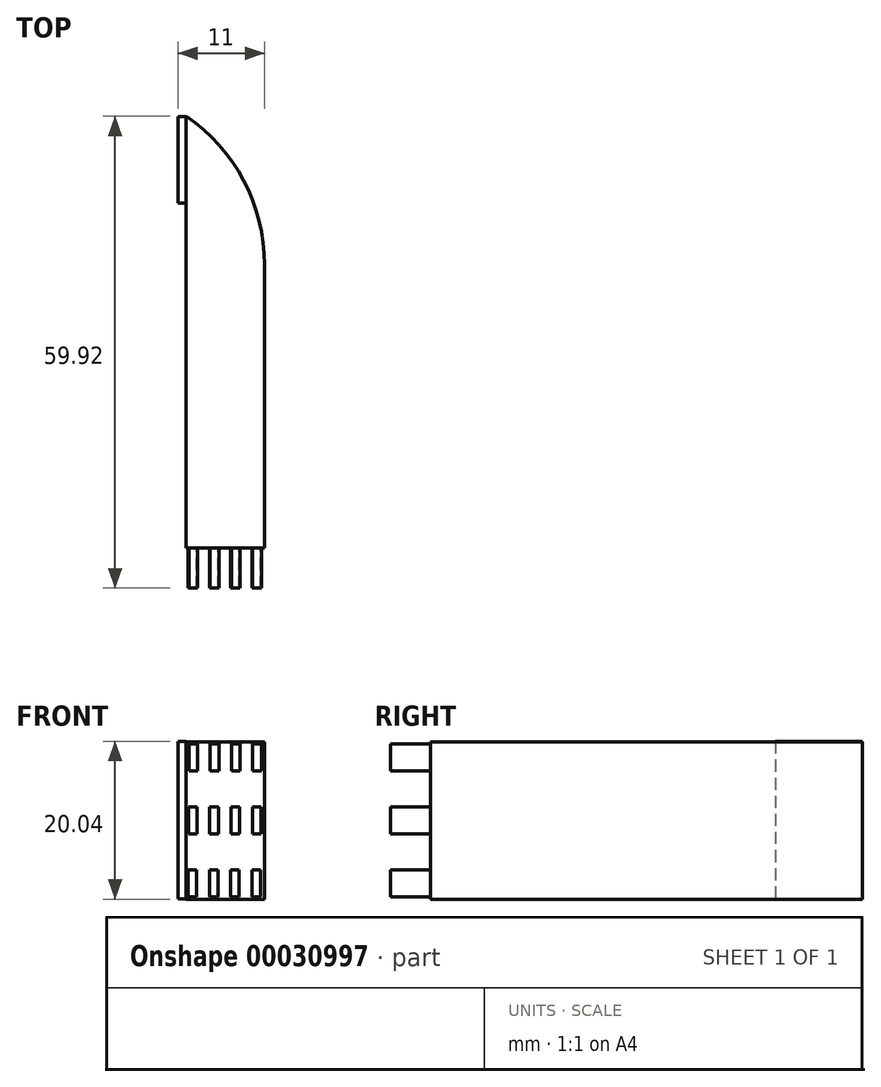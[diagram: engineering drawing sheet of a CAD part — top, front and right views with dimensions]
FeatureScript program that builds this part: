
annotation { "Feature Type Name" : "Feature", "Feature Type Description" : "" }
export const myFeature = defineFeature(function(context is Context, id is Id, definition is map)
    precondition{}
    {
        {
            var Q0;
            Q0=qCreatedBy(makeId("Front.planeOp"),FACE);
            var sketch = newSketch(context, id + "F0", { "sketchPlane" : qUnion([Q0])});
            skLineSegment(sketch, "E0.rect.bottom", {"start": v(-5, 10) * mm, "end": v(5, 10) * mm});
            skLineSegment(sketch, "E0.rect.top", {"start": v(-5, -10) * mm, "end": v(5, -10) * mm});
            skLineSegment(sketch, "E0.rect.left", {"start": v(-5, 10) * mm, "end": v(-5, -10) * mm});
            skLineSegment(sketch, "E0.rect.right", {"start": v(5, 10) * mm, "end": v(5, -10) * mm});
            skPoint(sketch, "E0.rect.middle", {"position": v(0, 0) * mm});
            skSolve(sketch);
        }
        {
            var Q0;
            Q0 = qSketchRegion(id + "F0", true);
            extrude(context, id + "F1", {"entities" : qUnion([Q0]), "oppositeDirection" : true, "depth" : 25 * mm});
        }
        {
            var Q0;
            Q0=makeQuery(id+"F1.opExtrude","CAP_EDGE",EDGE,{"disambiguationData":[OSD([sQuery(id+"F0.wireOp",EDGE,"E0.rect.left")])],"isStart":false});
            cPlane(context, id + "F2", {"entities" : qUnion([Q0]), "cplaneType" : CPlaneType.LINE_ANGLE, "offset" : 150 * mm, "angle" : 0 * degree, "width" : 150 * mm, "height" : 150 * mm});
        }
        {
            var Q0;
            Q0=qCreatedBy(id+"F2.planeOp",FACE);
            var sketch = newSketch(context, id + "F3", { "sketchPlane" : qUnion([Q0])});
            skLineSegment(sketch, "E1.rect.bottom", {"start": v(-54.87, 10) * mm, "end": v(-24.87, 10) * mm});
            skLineSegment(sketch, "E1.rect.top", {"start": v(-54.87, -10) * mm, "end": v(-24.87, -10) * mm});
            skLineSegment(sketch, "E1.rect.left", {"start": v(-54.87, 10) * mm, "end": v(-54.87, -10) * mm});
            skLineSegment(sketch, "E1.rect.right", {"start": v(-24.87, 10) * mm, "end": v(-24.87, -10) * mm});
            skPoint(sketch, "E1.rect.middle", {"position": v(-39.87, 0) * mm});
            skSolve(sketch);
        }
        {
            var Q0;
            Q0=makeQuery(id+"F3.imprint","IMPRINT",FACE,{"disambiguationData":[TD([[makeQuery(id+"F3.imprint","IMPRINT",EDGE,{"derivedFrom":sQuery(id+"F3.wireOp",EDGE,"E1.rect.bottom")}),-1.0]])]});
            extrude(context, id + "F4", {"entities" : qUnion([Q0]), "operationType" : NewBodyOperationType.ADD, "oppositeDirection" : true, "depth" : 10 * mm});
        }
        {
            var Q0;
            Q0=makeQuery(id+"F4.opExtrude","CAP_EDGE",EDGE,{"disambiguationData":[OSD([sQuery(id+"F3.wireOp",EDGE,"E1.rect.left")])],"isStart":false});
            fillet(context, id + "F5", {"entities" : qUnion([Q0]), "radius" : 22.72 * mm, "tangentPropagation" : true, "allowEdgeOverflow" : false});
        }
        {
            var Q0;
            Q0=qCreatedBy(id+"F2.planeOp",FACE);
            var sketch = newSketch(context, id + "F6", { "sketchPlane" : qUnion([Q0])});
            skLineSegment(sketch, "E2.bottom", {"start": v(-54.82, 10.04) * mm, "end": v(-43.82, 10.04) * mm});
            skLineSegment(sketch, "E2.top", {"start": v(-54.82, -9.96) * mm, "end": v(-43.82, -9.96) * mm});
            skLineSegment(sketch, "E2.left", {"start": v(-54.82, 10.04) * mm, "end": v(-54.82, -9.96) * mm});
            skLineSegment(sketch, "E2.right", {"start": v(-43.82, 10.04) * mm, "end": v(-43.82, -9.96) * mm});
            skSolve(sketch);
        }
        {
            var Q0;
            Q0=makeQuery(id+"F6.imprint","IMPRINT",FACE,{"disambiguationData":[TD([[makeQuery(id+"F6.imprint","IMPRINT",EDGE,{"derivedFrom":sQuery(id+"F6.wireOp",EDGE,"E2.bottom")}),-1.0]])]});
            extrude(context, id + "F7", {"entities" : qUnion([Q0]), "operationType" : NewBodyOperationType.ADD, "depth" : 1 * mm});
        }
        {
            var Q0;
            Q0=makeQuery(id+"F1.opExtrude","CAP_FACE",FACE,{"disambiguationData":[OSD([sQuery(id+"F0.wireOp",EDGE,"E0.rect.bottom"),sQuery(id+"F0.wireOp",EDGE,"E0.rect.top"),sQuery(id+"F0.wireOp",EDGE,"E0.rect.left"),sQuery(id+"F0.wireOp",EDGE,"E0.rect.right")])],"isStart":true});
            var sketch = newSketch(context, id + "F8", { "sketchPlane" : qUnion([Q0])});
            skLineSegment(sketch, "E3.bottom", {"start": v(-4.6, 9.7) * mm, "end": v(-3.5, 9.7) * mm});
            skLineSegment(sketch, "E3.top", {"start": v(-4.6, 6.3) * mm, "end": v(-3.5, 6.3) * mm});
            skLineSegment(sketch, "E3.left", {"start": v(-4.6, 9.7) * mm, "end": v(-4.6, 6.3) * mm});
            skLineSegment(sketch, "E3.right", {"start": v(-3.5, 9.7) * mm, "end": v(-3.5, 6.3) * mm});
            skLineSegment(sketch, "E4.1.0.0", {"start": v(-0.8, 9.7) * mm, "end": v(-0.8, 6.3) * mm});
            skLineSegment(sketch, "E4.1.0.1", {"start": v(-1.9, 9.7) * mm, "end": v(-0.8, 9.7) * mm});
            skLineSegment(sketch, "E4.1.0.2", {"start": v(-1.9, 9.7) * mm, "end": v(-1.9, 6.3) * mm});
            skLineSegment(sketch, "E4.1.0.3", {"start": v(-1.9, 6.3) * mm, "end": v(-0.8, 6.3) * mm});
            skLineSegment(sketch, "E4.2.0.0", {"start": v(1.9, 9.7) * mm, "end": v(1.9, 6.3) * mm});
            skLineSegment(sketch, "E4.2.0.1", {"start": v(0.8, 9.7) * mm, "end": v(1.9, 9.7) * mm});
            skLineSegment(sketch, "E4.2.0.2", {"start": v(0.8, 9.7) * mm, "end": v(0.8, 6.3) * mm});
            skLineSegment(sketch, "E4.2.0.3", {"start": v(0.8, 6.3) * mm, "end": v(1.9, 6.3) * mm});
            skLineSegment(sketch, "E4.3.0.0", {"start": v(4.6, 9.7) * mm, "end": v(4.6, 6.3) * mm});
            skLineSegment(sketch, "E4.3.0.1", {"start": v(3.5, 9.7) * mm, "end": v(4.6, 9.7) * mm});
            skLineSegment(sketch, "E4.3.0.2", {"start": v(3.5, 9.7) * mm, "end": v(3.5, 6.3) * mm});
            skLineSegment(sketch, "E4.3.0.3", {"start": v(3.5, 6.3) * mm, "end": v(4.6, 6.3) * mm});
            skLineSegment(sketch, "E4.direction1", {"start": v(-3.5, 6.3) * mm, "end": v(-0.8, 6.3) * mm, "construction": true});
            skLineSegment(sketch, "E5.1.0.0", {"start": v(-4.66, -1.7) * mm, "end": v(-3.56, -1.7) * mm});
            skLineSegment(sketch, "E5.1.0.1", {"start": v(-4.66, 1.7) * mm, "end": v(-4.66, -1.7) * mm});
            skLineSegment(sketch, "E5.1.0.2", {"start": v(-3.56, 1.7) * mm, "end": v(-3.56, -1.7) * mm});
            skLineSegment(sketch, "E5.1.0.3", {"start": v(-4.66, 1.7) * mm, "end": v(-3.56, 1.7) * mm});
            skLineSegment(sketch, "E5.2.0.0", {"start": v(-4.72, -9.7) * mm, "end": v(-3.62, -9.7) * mm});
            skLineSegment(sketch, "E5.2.0.1", {"start": v(-4.72, -6.3) * mm, "end": v(-4.72, -9.7) * mm});
            skLineSegment(sketch, "E5.2.0.2", {"start": v(-3.62, -6.3) * mm, "end": v(-3.62, -9.7) * mm});
            skLineSegment(sketch, "E5.2.0.3", {"start": v(-4.72, -6.3) * mm, "end": v(-3.62, -6.3) * mm});
            skLineSegment(sketch, "E5.direction1", {"start": v(-4.6, 6.3) * mm, "end": v(-4.66, -1.7) * mm, "construction": true});
            skLineSegment(sketch, "E6.1.0.0", {"start": v(-1.96, 1.7) * mm, "end": v(-1.96, -1.7) * mm});
            skLineSegment(sketch, "E6.1.0.1", {"start": v(-1.96, -1.7) * mm, "end": v(-0.86, -1.7) * mm});
            skLineSegment(sketch, "E6.1.0.2", {"start": v(-0.86, 1.7) * mm, "end": v(-0.86, -1.7) * mm});
            skLineSegment(sketch, "E6.1.0.3", {"start": v(-1.96, 1.7) * mm, "end": v(-0.86, 1.7) * mm});
            skLineSegment(sketch, "E6.2.0.0", {"start": v(-2.02, -6.3) * mm, "end": v(-2.02, -9.7) * mm});
            skLineSegment(sketch, "E6.2.0.1", {"start": v(-2.02, -9.7) * mm, "end": v(-0.92, -9.7) * mm});
            skLineSegment(sketch, "E6.2.0.2", {"start": v(-0.92, -6.3) * mm, "end": v(-0.92, -9.7) * mm});
            skLineSegment(sketch, "E6.2.0.3", {"start": v(-2.02, -6.3) * mm, "end": v(-0.92, -6.3) * mm});
            skLineSegment(sketch, "E6.direction1", {"start": v(-1.9, 6.3) * mm, "end": v(-1.96, -1.7) * mm, "construction": true});
            skLineSegment(sketch, "E7.1.0.0", {"start": v(1.84, 1.7) * mm, "end": v(1.84, -1.7) * mm});
            skLineSegment(sketch, "E7.1.0.1", {"start": v(0.74, 1.7) * mm, "end": v(0.74, -1.7) * mm});
            skLineSegment(sketch, "E7.1.0.2", {"start": v(0.74, 1.7) * mm, "end": v(1.84, 1.7) * mm});
            skLineSegment(sketch, "E7.1.0.3", {"start": v(0.74, -1.7) * mm, "end": v(1.84, -1.7) * mm});
            skLineSegment(sketch, "E7.2.0.0", {"start": v(1.78, -6.3) * mm, "end": v(1.78, -9.7) * mm});
            skLineSegment(sketch, "E7.2.0.1", {"start": v(0.68, -6.3) * mm, "end": v(0.68, -9.7) * mm});
            skLineSegment(sketch, "E7.2.0.2", {"start": v(0.68, -6.3) * mm, "end": v(1.78, -6.3) * mm});
            skLineSegment(sketch, "E7.2.0.3", {"start": v(0.68, -9.7) * mm, "end": v(1.78, -9.7) * mm});
            skLineSegment(sketch, "E7.direction1", {"start": v(1.9, 6.3) * mm, "end": v(1.84, -1.7) * mm, "construction": true});
            skLineSegment(sketch, "E8.1.0.0", {"start": v(3.44, 1.7) * mm, "end": v(3.44, -1.7) * mm});
            skLineSegment(sketch, "E8.1.0.1", {"start": v(3.44, -1.7) * mm, "end": v(4.54, -1.7) * mm});
            skLineSegment(sketch, "E8.1.0.2", {"start": v(4.54, 1.7) * mm, "end": v(4.54, -1.7) * mm});
            skLineSegment(sketch, "E8.1.0.3", {"start": v(3.44, 1.7) * mm, "end": v(4.54, 1.7) * mm});
            skLineSegment(sketch, "E8.2.0.0", {"start": v(3.38, -6.3) * mm, "end": v(3.38, -9.7) * mm});
            skLineSegment(sketch, "E8.2.0.1", {"start": v(3.38, -9.7) * mm, "end": v(4.48, -9.7) * mm});
            skLineSegment(sketch, "E8.2.0.2", {"start": v(4.48, -6.3) * mm, "end": v(4.48, -9.7) * mm});
            skLineSegment(sketch, "E8.2.0.3", {"start": v(3.38, -6.3) * mm, "end": v(4.48, -6.3) * mm});
            skLineSegment(sketch, "E8.direction1", {"start": v(3.5, 6.3) * mm, "end": v(3.44, -1.7) * mm, "construction": true});
            skSolve(sketch);
        }
        {
            var Q0;
            Q0 = qSketchRegion(id + "F8", true);
            extrude(context, id + "F9", {"entities" : qUnion([Q0]), "operationType" : NewBodyOperationType.ADD, "depth" : 5.05 * mm});
        }
    });
